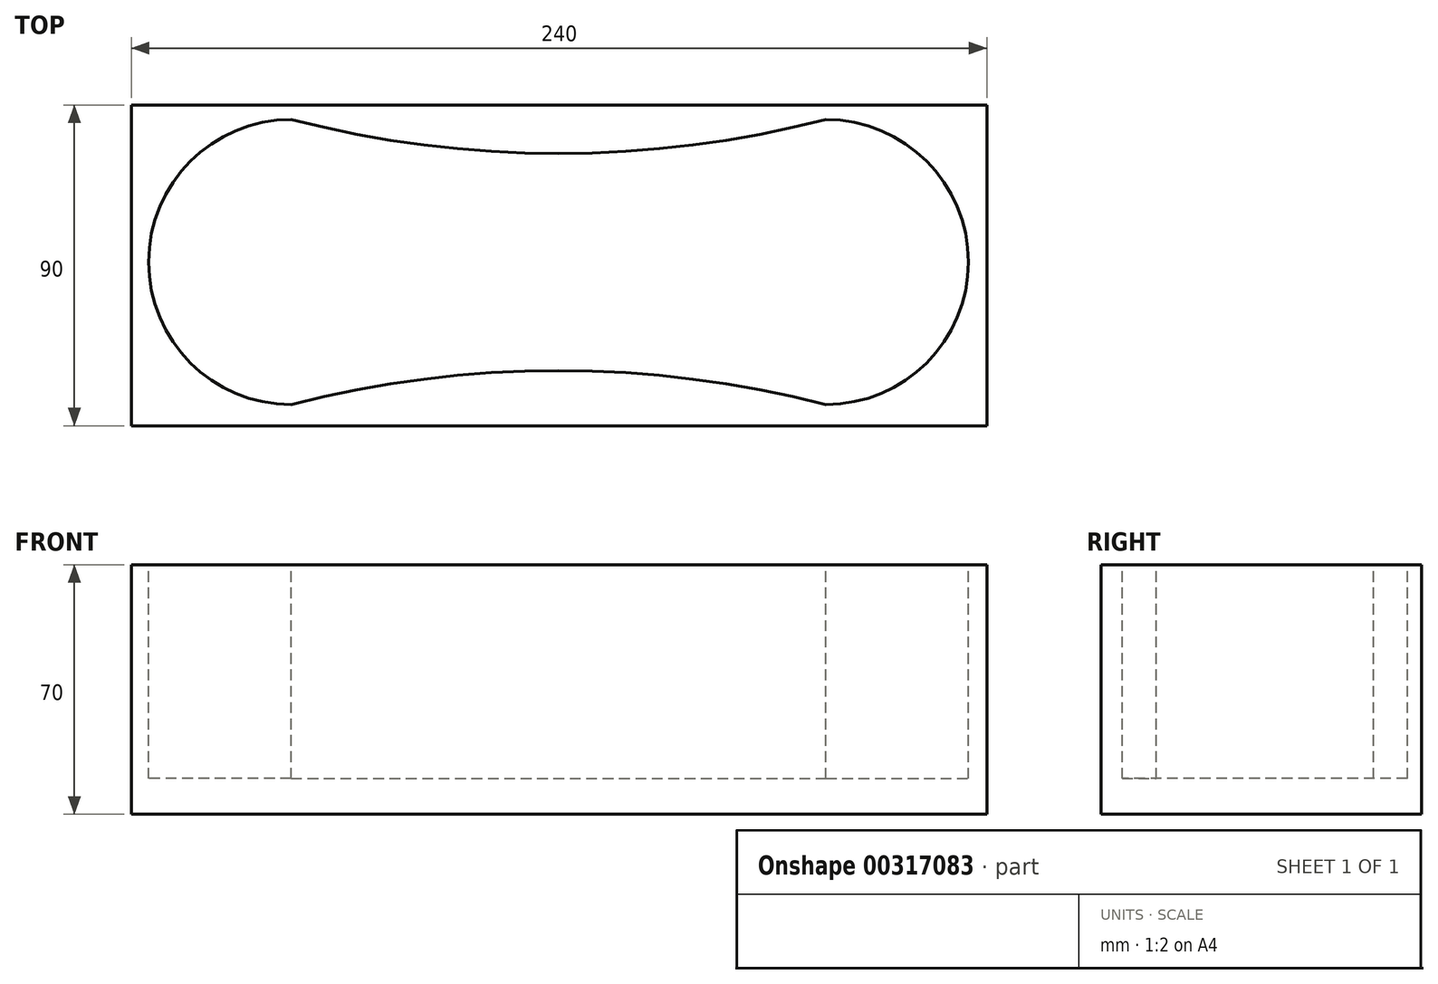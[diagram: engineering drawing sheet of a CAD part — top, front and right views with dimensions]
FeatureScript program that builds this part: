
annotation { "Feature Type Name" : "Feature", "Feature Type Description" : "" }
export const myFeature = defineFeature(function(context is Context, id is Id, definition is map)
    precondition{}
    {
        {
            var Q0;
            Q0=qCreatedBy(makeId("Front.planeOp"),FACE);
            var sketch = newSketch(context, id + "F0", { "sketchPlane" : qUnion([Q0])});
            skLineSegment(sketch, "E0.bottom", {"start": v(120, 35) * mm, "end": v(-120, 35) * mm});
            skLineSegment(sketch, "E0.top", {"start": v(120, -35) * mm, "end": v(-120, -35) * mm});
            skLineSegment(sketch, "E0.left", {"start": v(120, 35) * mm, "end": v(120, -35) * mm});
            skLineSegment(sketch, "E0.right", {"start": v(-120, 35) * mm, "end": v(-120, -35) * mm});
            skPoint(sketch, "E0.middle", {"position": v(0, 0) * mm});
            skSolve(sketch);
        }
        {
            var Q0;
            Q0 = qSketchRegion(id + "F0", true);
            extrude(context, id + "F1", {"entities" : qUnion([Q0]), "depth" : 45 * mm, "offsetDistance" : 25 * mm});
        }
        {
            var Q0;
            Q0=makeQuery(id+"F1.opExtrude","CAP_FACE",FACE,{"disambiguationData":[OSD([sQuery(id+"F0.wireOp",EDGE,"E0.bottom"),sQuery(id+"F0.wireOp",EDGE,"E0.top"),sQuery(id+"F0.wireOp",EDGE,"E0.left"),sQuery(id+"F0.wireOp",EDGE,"E0.right")])],"isStart":true});
            extrude(context, id + "F2", {"entities" : qUnion([Q0]), "operationType" : NewBodyOperationType.ADD, "depth" : 45 * mm, "offsetDistance" : 25 * mm});
        }
        {
            var Q0;
            Q0=qCreatedBy(makeId("Top.planeOp"),FACE);
            cPlane(context, id + "F3", {"entities" : qUnion([Q0]), "cplaneType" : CPlaneType.OFFSET, "offset" : 35 * mm, "width" : 150 * mm, "height" : 150 * mm});
        }
        {
            var Q0;
            Q0=qCreatedBy(id+"F3.planeOp",FACE);
            var sketch = newSketch(context, id + "F4", { "sketchPlane" : qUnion([Q0])});
            skArc(sketch, "E1", {"start": v(74.82, -39.04) * mm, "mid": v(114.82, 0.96) * mm, "end": v(74.82, 40.96) * mm});
            skArc(sketch, "E2", {"start": v(-75.18, 40.96) * mm, "mid": v(-115.18, 0.96) * mm, "end": v(-75.18, -39.04) * mm});
            skArc(sketch, "E3", {"start": v(-75.18, 40.96) * mm, "mid": v(-0.18, 31.43) * mm, "end": v(74.82, 40.96) * mm});
            skArc(sketch, "E4", {"start": v(74.82, -39.04) * mm, "mid": v(-0.18, -29.51) * mm, "end": v(-75.18, -39.04) * mm});
            skSolve(sketch);
        }
        {
            var Q0;
            Q0 = qSketchRegion(id + "F4", true);
            extrude(context, id + "F5", {"entities" : qUnion([Q0]), "operationType" : NewBodyOperationType.REMOVE, "oppositeDirection" : true, "depth" : 60 * mm, "offsetDistance" : 25 * mm});
        }
    });
